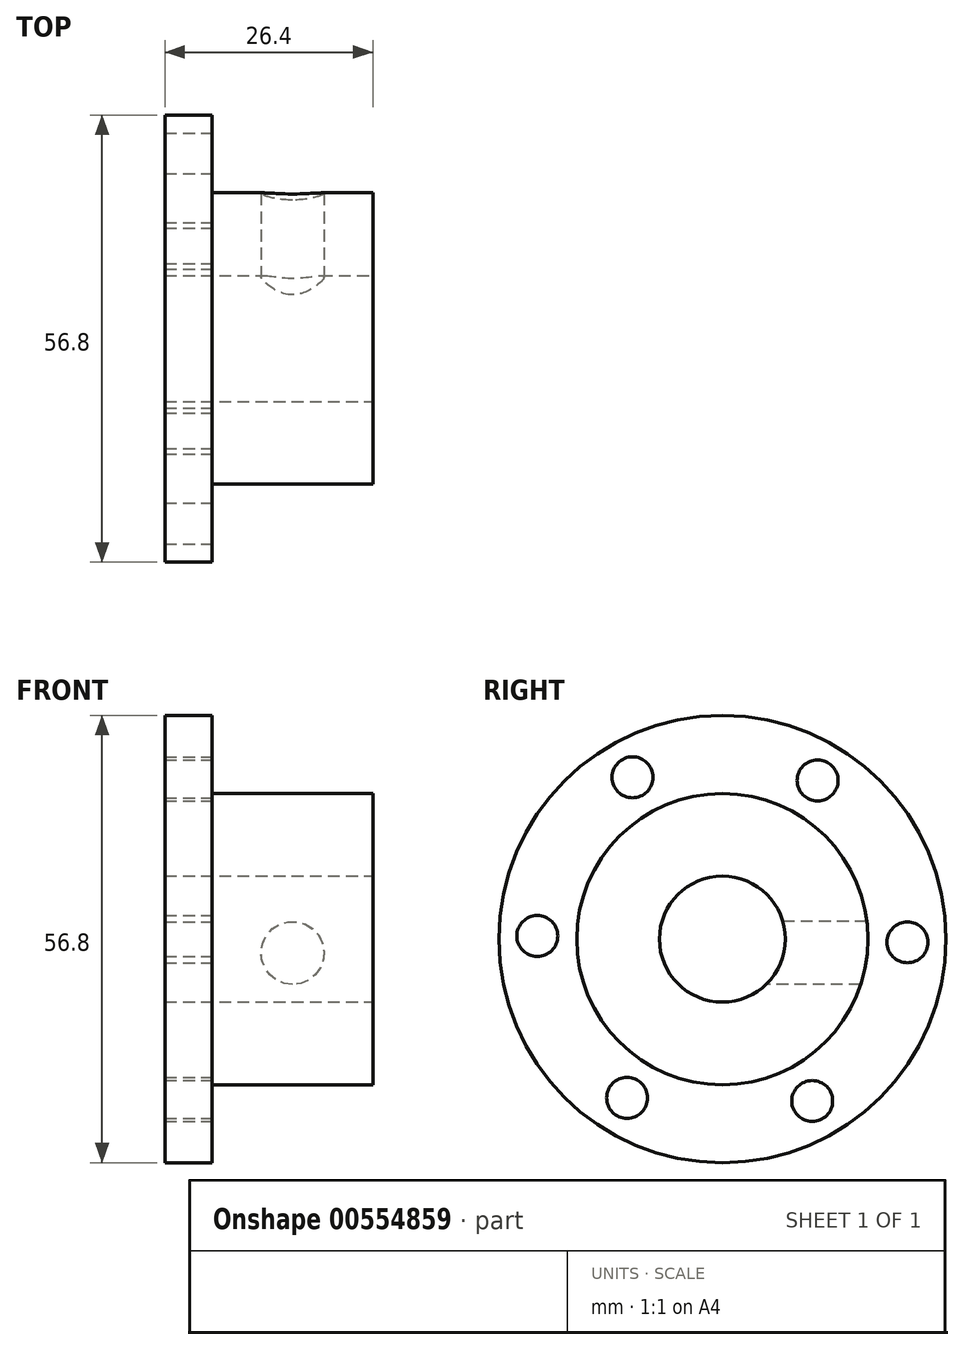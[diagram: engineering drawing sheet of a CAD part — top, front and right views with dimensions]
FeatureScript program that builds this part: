
annotation { "Feature Type Name" : "Feature", "Feature Type Description" : "" }
export const myFeature = defineFeature(function(context is Context, id is Id, definition is map)
    precondition{}
    {
        {
            var Q0;
            Q0=qCreatedBy(makeId("Front.planeOp"),FACE);
            var sketch = newSketch(context, id + "F0", { "sketchPlane" : qUnion([Q0])});
            skLineSegment(sketch, "E0", {"start": v(-32.64, -20.56) * mm, "end": v(32.64, -20.56) * mm});
            skLineSegment(sketch, "E1", {"start": v(32.64, -20.56) * mm, "end": v(-32.64, -20.56) * mm});
            skLineSegment(sketch, "E2", {"start": v(-32.64, -12.56) * mm, "end": v(-6.24, -12.56) * mm});
            skLineSegment(sketch, "E3", {"start": v(-32.64, -12.56) * mm, "end": v(-32.64, 7.84) * mm});
            skLineSegment(sketch, "E4", {"start": v(-32.64, 7.84) * mm, "end": v(-26.64, 7.84) * mm});
            skLineSegment(sketch, "E5", {"start": v(-6.24, -12.56) * mm, "end": v(-6.24, -2.06) * mm});
            skLineSegment(sketch, "E6", {"start": v(-26.64, 7.84) * mm, "end": v(-26.64, -2.06) * mm});
            skLineSegment(sketch, "E7", {"start": v(-26.64, -2.06) * mm, "end": v(-6.24, -2.06) * mm});
            skSolve(sketch);
        }
        {
            var Q0;
            Q0 = qSketchRegion(id + "F0", true);
            var Q1;
            Q1=sQuery(id+"F0.wireOp",EDGE,"E1");
            revolve(context, id + "F1", {"entities" : qUnion([Q0]), "axis" : qUnion([Q1]), "revolveType" : RevolveType.FULL});
        }
        {
            var Q0;
            Q0=makeQuery(id+"F1.opRevolve","SWEPT_FACE",FACE,{"disambiguationData":[OSD([sQuery(id+"F0.wireOp",EDGE,"E6")])]});
            var sketch = newSketch(context, id + "F2", { "sketchPlane" : qUnion([Q0])});
            skCircle(sketch, "E8", {"center": v(0, -20.56) * mm, "radius": 23.52 * mm});
            skCircle(sketch, "E9", {"center": v(-11.41, 0) * mm, "radius": 2.6 * mm});
            skCircle(sketch, "E10.1.0", {"center": v(-23.52, -20.17) * mm, "radius": 2.6 * mm});
            skCircle(sketch, "E10.2.0", {"center": v(-12.1, -40.73) * mm, "radius": 2.6 * mm});
            skCircle(sketch, "E10.3.0", {"center": v(11.41, -41.13) * mm, "radius": 2.6 * mm});
            skCircle(sketch, "E10.4.0", {"center": v(23.52, -20.96) * mm, "radius": 2.6 * mm});
            skCircle(sketch, "E10.5.0", {"center": v(12.1, -0.4) * mm, "radius": 2.6 * mm});
            skSolve(sketch);
        }
        {
            var Q0;
            Q0=sQuery(id+"F2.wireOp",VERTEX,"E9.center");
            var Q1;
            Q1=sQuery(id+"F2.wireOp",VERTEX,"E10.5.0.center");
            var Q2;
            Q2=sQuery(id+"F2.wireOp",VERTEX,"E10.4.0.center");
            var Q3;
            Q3=sQuery(id+"F2.wireOp",VERTEX,"E10.3.0.center");
            var Q4;
            Q4=sQuery(id+"F2.wireOp",VERTEX,"E10.2.0.center");
            var Q5;
            Q5=sQuery(id+"F2.wireOp",VERTEX,"E10.1.0.center");
            var Q6;
            Q6=makeQuery(id+"F1.opRevolve","SWEPT_BODY",BODY,{"disambiguationData":[OSD([sQuery(id+"F0.wireOp",EDGE,"E2"),sQuery(id+"F0.wireOp",EDGE,"E3"),sQuery(id+"F0.wireOp",EDGE,"E4"),sQuery(id+"F0.wireOp",EDGE,"E5"),sQuery(id+"F0.wireOp",EDGE,"E6"),sQuery(id+"F0.wireOp",EDGE,"oNjWnfSY-uWGl-p5sd-NiaE-xDCx2udgH694")])]});
            hole(context, id + "F3", {"style" : HoleStyle.SIMPLE, "endStyle" : HoleEndStyle.THROUGH, "holeDiameter" : 5.2 * mm, "isTappedThrough" : true, "tappedDepth" : 12 * mm, "tapClearance" : 3, "locations" : qUnion([Q0, Q1, Q2, Q3, Q4, Q5]), "scope" : qUnion([Q6])});
        }
        {
            var Q0;
            Q0=qCreatedBy(makeId("Front.planeOp"),FACE);
            var sketch = newSketch(context, id + "F4", { "sketchPlane" : qUnion([Q0])});
            skCircle(sketch, "E11", {"center": v(-16.44, -22.32) * mm, "radius": 4 * mm});
            skSolve(sketch);
        }
        {
            var Q0;
            Q0=sQuery(id+"F4.wireOp",VERTEX,"E11.center");
            var Q1;
            Q1=makeQuery(id+"F1.opRevolve","SWEPT_BODY",BODY,{"disambiguationData":[OSD([sQuery(id+"F0.wireOp",EDGE,"E2"),sQuery(id+"F0.wireOp",EDGE,"E3"),sQuery(id+"F0.wireOp",EDGE,"E4"),sQuery(id+"F0.wireOp",EDGE,"E5"),sQuery(id+"F0.wireOp",EDGE,"E6"),sQuery(id+"F0.wireOp",EDGE,"E7")])]});
            hole(context, id + "F5", {"style" : HoleStyle.SIMPLE, "endStyle" : HoleEndStyle.THROUGH, "holeDiameter" : 8 * mm, "isTappedThrough" : true, "tappedDepth" : 12 * mm, "tapClearance" : 3, "locations" : qUnion([Q0]), "scope" : qUnion([Q1])});
        }
    });
